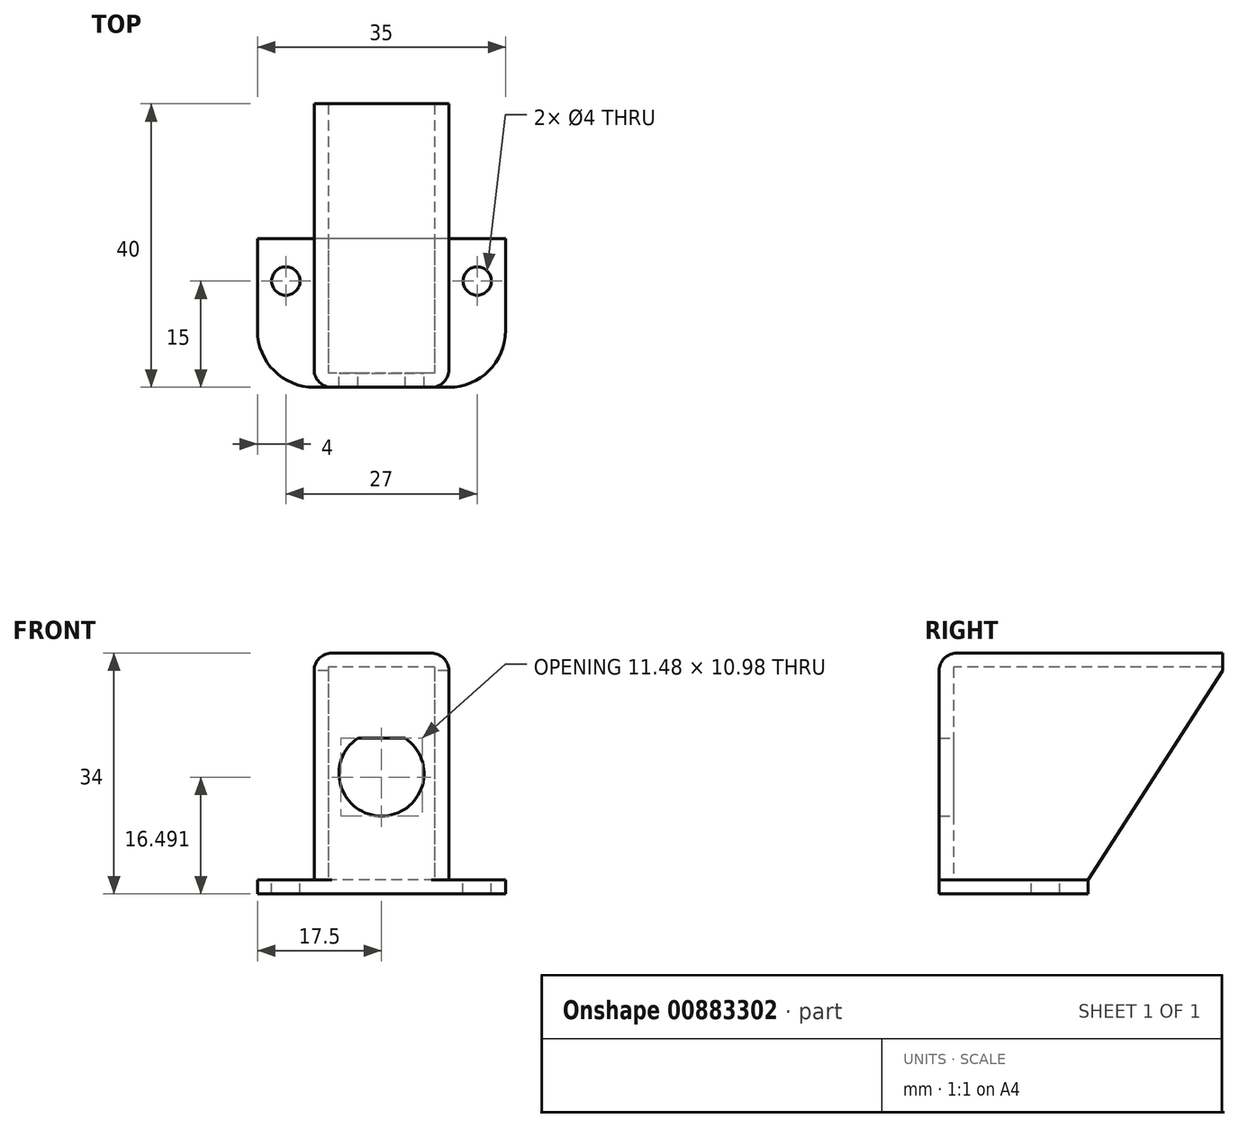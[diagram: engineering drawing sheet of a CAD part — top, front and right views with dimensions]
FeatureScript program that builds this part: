
annotation { "Feature Type Name" : "Feature", "Feature Type Description" : "" }
export const myFeature = defineFeature(function(context is Context, id is Id, definition is map)
    precondition{}
    {
        {
            var Q0;
            Q0=qCreatedBy(makeId("Front.planeOp"),FACE);
            var sketch = newSketch(context, id + "F0", { "sketchPlane" : qUnion([Q0])});
            skCircle(sketch, "E0", {"center": v(0, 0) * mm, "radius": 6 * mm});
            skLineSegment(sketch, "E1", {"start": v(-3.34, 4.98) * mm, "end": v(3.34, 4.98) * mm});
            skLineSegment(sketch, "E2.bottom", {"start": v(7.5, 15) * mm, "end": v(-7.5, 15) * mm});
            skLineSegment(sketch, "E2.top", {"start": v(7.5, -15) * mm, "end": v(-7.5, -15) * mm});
            skLineSegment(sketch, "E2.left", {"start": v(7.5, 15) * mm, "end": v(7.5, -15) * mm});
            skLineSegment(sketch, "E2.right", {"start": v(-7.5, 15) * mm, "end": v(-7.5, -15) * mm});
            skLineSegment(sketch, "E3.bottom", {"start": v(9.5, 17) * mm, "end": v(-9.5, 17) * mm});
            skLineSegment(sketch, "E3.top", {"start": v(9.5, -17) * mm, "end": v(-9.5, -17) * mm});
            skLineSegment(sketch, "E3.left", {"start": v(9.5, 17) * mm, "end": v(9.5, -17) * mm});
            skLineSegment(sketch, "E3.right", {"start": v(-9.5, 17) * mm, "end": v(-9.5, -17) * mm});
            skLineSegment(sketch, "E4.bottom", {"start": v(9.5, -17) * mm, "end": v(17.5, -17) * mm});
            skLineSegment(sketch, "E4.top", {"start": v(9.5, -15) * mm, "end": v(17.5, -15) * mm});
            skLineSegment(sketch, "E4.left", {"start": v(9.5, -17) * mm, "end": v(9.5, -15) * mm});
            skLineSegment(sketch, "E4.right", {"start": v(17.5, -17) * mm, "end": v(17.5, -15) * mm});
            skLineSegment(sketch, "E5.bottom", {"start": v(-9.5, -17) * mm, "end": v(-17.5, -17) * mm});
            skLineSegment(sketch, "E5.top", {"start": v(-9.5, -15) * mm, "end": v(-17.5, -15) * mm});
            skLineSegment(sketch, "E5.left", {"start": v(-9.5, -17) * mm, "end": v(-9.5, -15) * mm});
            skLineSegment(sketch, "E5.right", {"start": v(-17.5, -17) * mm, "end": v(-17.5, -15) * mm});
            skSolve(sketch);
        }
        {
            var Q0;
            Q0 = qSketchRegion(id + "F0", true);
            var Q1;
            Q1=makeQuery(id+"F0.imprint","IMPRINT",FACE,{"disambiguationData":[TD([[makeQuery(id+"F0.imprint","IMPRINT",EDGE,{"derivedFrom":sQuery(id+"F0.wireOp",EDGE,"E2.bottom")}),1.0]])]});
            var Q2;
            {var subQ0=sQuery(id+"F0.wireOp",EDGE,"E1");Q2=makeQuery(id+"F0.imprint","IMPRINT",FACE,{"disambiguationData":[TD([[makeQuery(id+"F0.imprint","IMPRINT",EDGE,{"derivedFrom":subQ0}),1.0]])]});}
            extrude(context, id + "F1", {"entities" : qUnion([Q0, Q1, Q2]), "depth" : 2 * mm, "offsetDistance" : 25 * mm});
        }
        {
            var Q0;
            Q0 = qSketchRegion(id + "F0", true);
            extrude(context, id + "F2", {"entities" : qUnion([Q0]), "operationType" : NewBodyOperationType.ADD, "depth" : -38 * mm, "offsetDistance" : 25 * mm});
        }
        {
            var Q0;
            {var subQ0=sQuery(id+"F0.wireOp",EDGE,"E4.top");Q0=makeQuery(id+"F2.boolean.opBoolean","MERGE",FACE,{"derivedFrom":[makeQuery(id+"F1.opExtrude","SWEPT_FACE",FACE,{"disambiguationData":[OSD([subQ0])]}),makeQuery(id+"F2.opExtrude","SWEPT_FACE",FACE,{"disambiguationData":[OSD([subQ0])]})]});}
            cPlane(context, id + "F3", {"entities" : qUnion([Q0]), "cplaneType" : CPlaneType.OFFSET, "offset" : 0 * mm, "width" : 150 * mm, "height" : 150 * mm});
        }
        {
            var Q0;
            Q0=qCreatedBy(id+"F3.planeOp",FACE);
            var sketch = newSketch(context, id + "F4", { "sketchPlane" : qUnion([Q0])});
            skLineSegment(sketch, "E6.0.1", {"start": v(-9.5, 38) * mm, "end": v(-17.5, 38) * mm});
            skLineSegment(sketch, "E6.0.3", {"start": v(-17.5, -2) * mm, "end": v(-9.5, -2) * mm});
            skLineSegment(sketch, "E6.1.1", {"start": v(17.5, 38) * mm, "end": v(9.5, 38) * mm});
            skLineSegment(sketch, "E6.1.3", {"start": v(9.5, -2) * mm, "end": v(17.5, -2) * mm});
            skPoint(sketch, "E7", {"position": v(-13.5, 13) * mm});
            skPoint(sketch, "E8", {"position": v(13.5, 13) * mm});
            skLineSegment(sketch, "E9.bottom", {"start": v(-9.5, 19) * mm, "end": v(-17.5, 19) * mm});
            skLineSegment(sketch, "E9.top", {"start": v(-9.5, 7) * mm, "end": v(-17.5, 7) * mm});
            skLineSegment(sketch, "E9.left", {"start": v(-9.5, 19) * mm, "end": v(-9.5, 7) * mm});
            skLineSegment(sketch, "E9.right", {"start": v(-17.5, 19) * mm, "end": v(-17.5, 7) * mm});
            skLineSegment(sketch, "E10.bottom", {"start": v(17.5, 19) * mm, "end": v(9.5, 19) * mm});
            skLineSegment(sketch, "E10.top", {"start": v(17.5, 7) * mm, "end": v(9.5, 7) * mm});
            skLineSegment(sketch, "E10.left", {"start": v(17.5, 19) * mm, "end": v(17.5, 7) * mm});
            skLineSegment(sketch, "E10.right", {"start": v(9.5, 19) * mm, "end": v(9.5, 7) * mm});
            skLineSegment(sketch, "E11.bottom", {"start": v(-17.5, 38) * mm, "end": v(-9.5, 38) * mm});
            skLineSegment(sketch, "E11.top", {"start": v(-17.5, 19) * mm, "end": v(-9.5, 19) * mm});
            skLineSegment(sketch, "E11.left", {"start": v(-17.5, 38) * mm, "end": v(-17.5, 19) * mm});
            skLineSegment(sketch, "E11.right", {"start": v(-9.5, 38) * mm, "end": v(-9.5, 19) * mm});
            skLineSegment(sketch, "E12.bottom", {"start": v(9.5, 38) * mm, "end": v(17.5, 38) * mm});
            skLineSegment(sketch, "E12.top", {"start": v(9.5, 19) * mm, "end": v(17.5, 19) * mm});
            skLineSegment(sketch, "E12.left", {"start": v(9.5, 38) * mm, "end": v(9.5, 19) * mm});
            skLineSegment(sketch, "E12.right", {"start": v(17.5, 38) * mm, "end": v(17.5, 19) * mm});
            skSolve(sketch);
        }
        {
            var Q0;
            Q0=makeQuery(id+"F4.imprint","IMPRINT",FACE,{"disambiguationData":[TD([[makeQuery(id+"F4.imprint","IMPRINT",EDGE,{"derivedFrom":sQuery(id+"F4.wireOp",EDGE,"E6.0.1")}),1.0]])]});
            var Q1;
            Q1=makeQuery(id+"F4.imprint","IMPRINT",FACE,{"disambiguationData":[TD([[makeQuery(id+"F4.imprint","IMPRINT",EDGE,{"derivedFrom":sQuery(id+"F4.wireOp",EDGE,"E6.1.1")}),1.0]])]});
            extrude(context, id + "F5", {"entities" : qUnion([Q0, Q1]), "operationType" : NewBodyOperationType.REMOVE, "oppositeDirection" : true, "depth" : 25 * mm, "offsetDistance" : 25 * mm});
        }
        {
            var Q0;
            Q0=sQuery(id+"F4.wireOp",VERTEX,"E7");
            var Q1;
            Q1=sQuery(id+"F4.wireOp",VERTEX,"E8");
            var Q2;
            Q2=makeQuery(id+"F1.opExtrude","SWEPT_BODY",BODY,{"disambiguationData":[OSD([sQuery(id+"F0.wireOp",EDGE,"E0"),sQuery(id+"F0.wireOp",EDGE,"E1"),sQuery(id+"F0.wireOp",EDGE,"E3.bottom"),sQuery(id+"F0.wireOp",EDGE,"E3.top"),sQuery(id+"F0.wireOp",EDGE,"E3.left"),sQuery(id+"F0.wireOp",EDGE,"E3.right"),sQuery(id+"F0.wireOp",EDGE,"E4.bottom"),sQuery(id+"F0.wireOp",EDGE,"E4.top"),sQuery(id+"F0.wireOp",EDGE,"E4.right"),sQuery(id+"F0.wireOp",EDGE,"E5.bottom"),sQuery(id+"F0.wireOp",EDGE,"E5.top"),sQuery(id+"F0.wireOp",EDGE,"E5.right")])]});
            hole(context, id + "F6", {"style" : HoleStyle.SIMPLE, "endStyle" : HoleEndStyle.BLIND, "holeDiameter" : 4 * mm, "majorDiameter" : 5 * mm, "holeDepth" : 50 * mm, "isTappedThrough" : true, "tappedDepth" : 12 * mm, "tapClearance" : 3, "startFromSketch" : true, "locations" : qUnion([Q0, Q1]), "scope" : qUnion([Q2])});
        }
        {
            var Q0;
            Q0=makeQuery(id+"F5.boolean.opBoolean","MERGE",EDGE,{"derivedFrom":[makeQuery(id+"F1.opExtrude","CAP_EDGE",EDGE,{"disambiguationData":[OSD([sQuery(id+"F0.wireOp",EDGE,"E3.left")])],"isStart":false})],"fromTools":[makeQuery(id+"F5.opExtrude","SWEPT_EDGE",EDGE,{"disambiguationData":[OSD([sQuery(id+"F4.wireOp",EDGE,"E6.1.2"),sQuery(id+"F4.wireOp",EDGE,"E6.1.3")])]})]});
            var Q1;
            Q1=makeQuery(id+"F5.boolean.opBoolean","MERGE",EDGE,{"derivedFrom":[makeQuery(id+"F1.opExtrude","CAP_EDGE",EDGE,{"disambiguationData":[OSD([sQuery(id+"F0.wireOp",EDGE,"E3.right")])],"isStart":false})],"fromTools":[makeQuery(id+"F5.opExtrude","SWEPT_EDGE",EDGE,{"disambiguationData":[OSD([sQuery(id+"F4.wireOp",EDGE,"E6.0.0"),sQuery(id+"F4.wireOp",EDGE,"E6.0.3")])]})]});
            var Q2;
            {var subQ0=sQuery(id+"F0.wireOp",EDGE,"E3.right");var subQ1=sQuery(id+"F0.wireOp",EDGE,"E3.bottom");Q2=makeQuery(id+"F2.boolean.opBoolean","MERGE",EDGE,{"derivedFrom":[makeQuery(id+"F1.opExtrude","SWEPT_EDGE",EDGE,{"disambiguationData":[OSD([subQ1,subQ0])]}),makeQuery(id+"F2.opExtrude","SWEPT_EDGE",EDGE,{"disambiguationData":[OSD([subQ1,subQ0])]})]});}
            var Q3;
            {var subQ0=sQuery(id+"F0.wireOp",EDGE,"E3.left");var subQ1=sQuery(id+"F0.wireOp",EDGE,"E3.bottom");Q3=makeQuery(id+"F2.boolean.opBoolean","MERGE",EDGE,{"derivedFrom":[makeQuery(id+"F1.opExtrude","SWEPT_EDGE",EDGE,{"disambiguationData":[OSD([subQ1,subQ0])]}),makeQuery(id+"F2.opExtrude","SWEPT_EDGE",EDGE,{"disambiguationData":[OSD([subQ1,subQ0])]})]});}
            var Q4;
            Q4=makeQuery(id+"F1.opExtrude","CAP_EDGE",EDGE,{"disambiguationData":[OSD([sQuery(id+"F0.wireOp",EDGE,"E3.bottom")])],"isStart":false});
            var Q5;
            Q5=makeQuery(id+"F1.opExtrude","CAP_EDGE",EDGE,{"disambiguationData":[OSD([sQuery(id+"F0.wireOp",EDGE,"E3.right")])],"isStart":false});
            var Q6;
            Q6=makeQuery(id+"F1.opExtrude","CAP_EDGE",EDGE,{"disambiguationData":[OSD([sQuery(id+"F0.wireOp",EDGE,"E3.left")])],"isStart":false});
            var Q7;
            Q7=makeQuery(id+"F5.boolean.opBoolean","COPY",EDGE,{"derivedFrom":makeQuery(id+"F5.opExtrude","SWEPT_EDGE",EDGE,{"disambiguationData":[OSD([sQuery(id+"F4.wireOp",EDGE,"E10.bottom"),sQuery(id+"F4.wireOp",EDGE,"E10.left"),sQuery(id+"F4.wireOp",EDGE,"E12.right")])]})});
            var Q8;
            Q8=makeQuery(id+"F5.boolean.opBoolean","COPY",EDGE,{"derivedFrom":makeQuery(id+"F5.opExtrude","SWEPT_EDGE",EDGE,{"disambiguationData":[OSD([sQuery(id+"F4.wireOp",EDGE,"E9.bottom"),sQuery(id+"F4.wireOp",EDGE,"E9.right"),sQuery(id+"F4.wireOp",EDGE,"E11.left")])]})});
            fillet(context, id + "F7", {"entities" : qUnion([Q0, Q1, Q2, Q3, Q4, Q5, Q6, Q7, Q8]), "tangentPropagation" : true, "radius" : 2.5 * mm, "defaultsChanged" : false, "vertexSettings" : [], "allowEdgeOverflow" : false});
        }
        {
            var Q0;
            Q0=makeQuery(id+"F1.opExtrude","CAP_EDGE",EDGE,{"disambiguationData":[OSD([sQuery(id+"F0.wireOp",EDGE,"E5.right")])],"isStart":false});
            var Q1;
            Q1=makeQuery(id+"F1.opExtrude","CAP_EDGE",EDGE,{"disambiguationData":[OSD([sQuery(id+"F0.wireOp",EDGE,"E4.right")])],"isStart":false});
            fillet(context, id + "F8", {"entities" : qUnion([Q0, Q1]), "tangentPropagation" : true, "radius" : 8 * mm, "defaultsChanged" : true, "vertexSettings" : [], "allowEdgeOverflow" : false});
        }
        {
            var Q0;
            {var subQ0=sQuery(id+"F0.wireOp",EDGE,"E3.right");Q0=makeQuery(id+"F5.boolean.opBoolean","MERGE",FACE,{"derivedFrom":[makeQuery(id+"F2.boolean.opBoolean","MERGE",FACE,{"derivedFrom":[makeQuery(id+"F1.opExtrude","SWEPT_FACE",FACE,{"disambiguationData":[OSD([subQ0])]}),makeQuery(id+"F2.opExtrude","SWEPT_FACE",FACE,{"disambiguationData":[OSD([subQ0])]})]})],"fromTools":[makeQuery(id+"F5.opExtrude","SWEPT_FACE",FACE,{"disambiguationData":[OSD([sQuery(id+"F4.wireOp",EDGE,"E11.right")])]})]});}
            var sketch = newSketch(context, id + "F9", { "sketchPlane" : qUnion([Q0])});
            skLineSegment(sketch, "E13", {"start": v(-38, 14.5) * mm, "end": v(-19, -15) * mm});
            skSolve(sketch);
        }
        {
            var Q0;
            Q0=makeQuery(id+"F9.imprint","IMPRINT",FACE,{"disambiguationData":[TD([[makeQuery(id+"F9.imprint","IMPRINT",EDGE,{"derivedFrom":sQuery(id+"F9.wireOp",EDGE,"E13")}),-1.0]])]});
            extrude(context, id + "F10", {"entities" : qUnion([Q0]), "operationType" : NewBodyOperationType.REMOVE, "oppositeDirection" : true, "depth" : 25 * mm, "offsetDistance" : 25 * mm});
        }
    });
